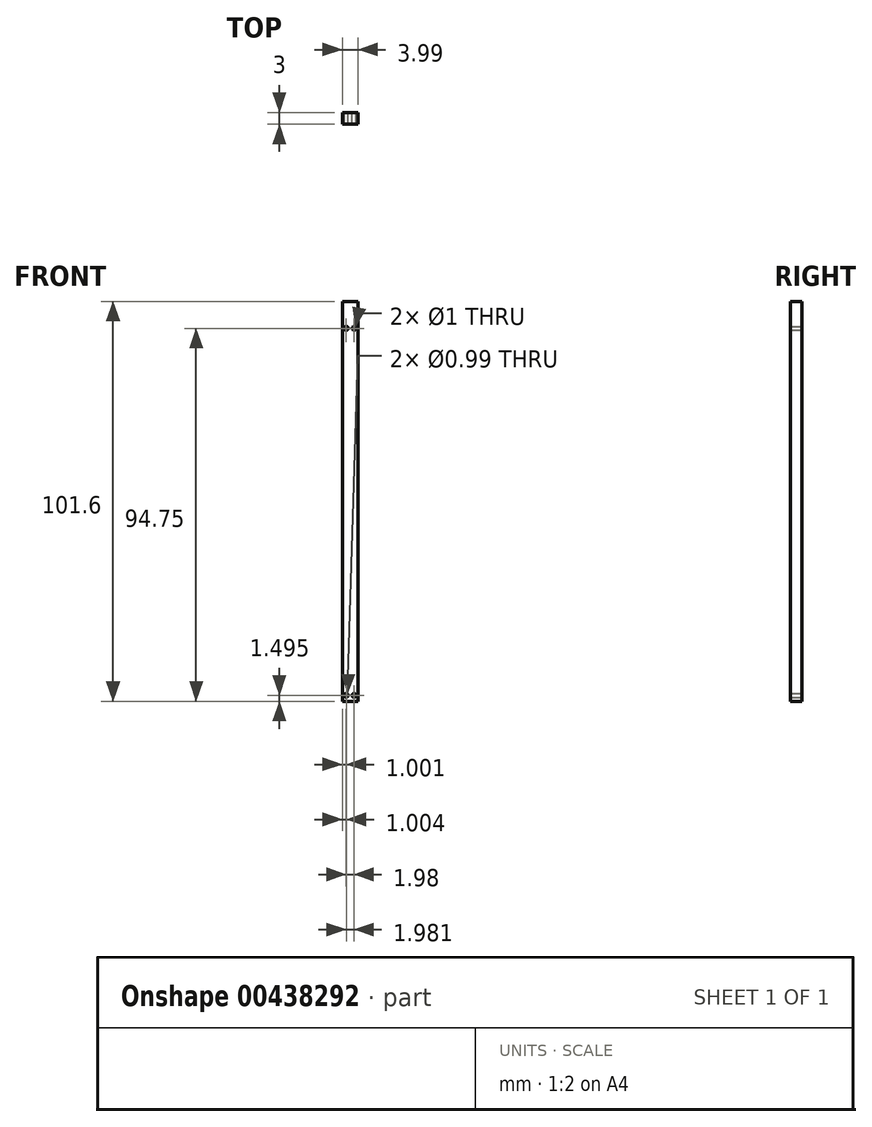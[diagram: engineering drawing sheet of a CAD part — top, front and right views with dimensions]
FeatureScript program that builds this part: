
annotation { "Feature Type Name" : "Feature", "Feature Type Description" : "" }
export const myFeature = defineFeature(function(context is Context, id is Id, definition is map)
    precondition{}
    {
        {
            var Q0;
            Q0=qCreatedBy(makeId("Front.planeOp"),FACE);
            var sketch = newSketch(context, id + "F0", { "sketchPlane" : qUnion([Q0])});
            skLineSegment(sketch, "E0.bottom", {"start": v(-23.03, 155.95) * mm, "end": v(-19.04, 155.95) * mm});
            skLineSegment(sketch, "E0.top", {"start": v(-23.03, 54.35) * mm, "end": v(-19.04, 54.35) * mm});
            skLineSegment(sketch, "E0.left", {"start": v(-23.03, 155.95) * mm, "end": v(-23.03, 54.35) * mm});
            skLineSegment(sketch, "E0.right", {"start": v(-19.04, 155.95) * mm, "end": v(-19.04, 54.35) * mm});
            skCircle(sketch, "E1", {"center": v(-22.03, 149.1) * mm, "radius": 0.5 * mm});
            skCircle(sketch, "E2", {"center": v(-20.05, 149.1) * mm, "radius": 0.5 * mm});
            skCircle(sketch, "E3", {"center": v(-22.03, 55.84) * mm, "radius": 0.5 * mm});
            skCircle(sketch, "E4", {"center": v(-20.04, 55.84) * mm, "radius": 0.5 * mm});
            skSolve(sketch);
        }
        {
            var Q0;
            Q0=makeQuery(id+"F0.imprint","IMPRINT",FACE,{"disambiguationData":[TD([[makeQuery(id+"F0.imprint","IMPRINT",EDGE,{"derivedFrom":sQuery(id+"F0.wireOp",EDGE,"E0.bottom")}),-1.0]])]});
            extrude(context, id + "F1", {"entities" : qUnion([Q0]), "depth" : 3 * mm});
        }
    });
